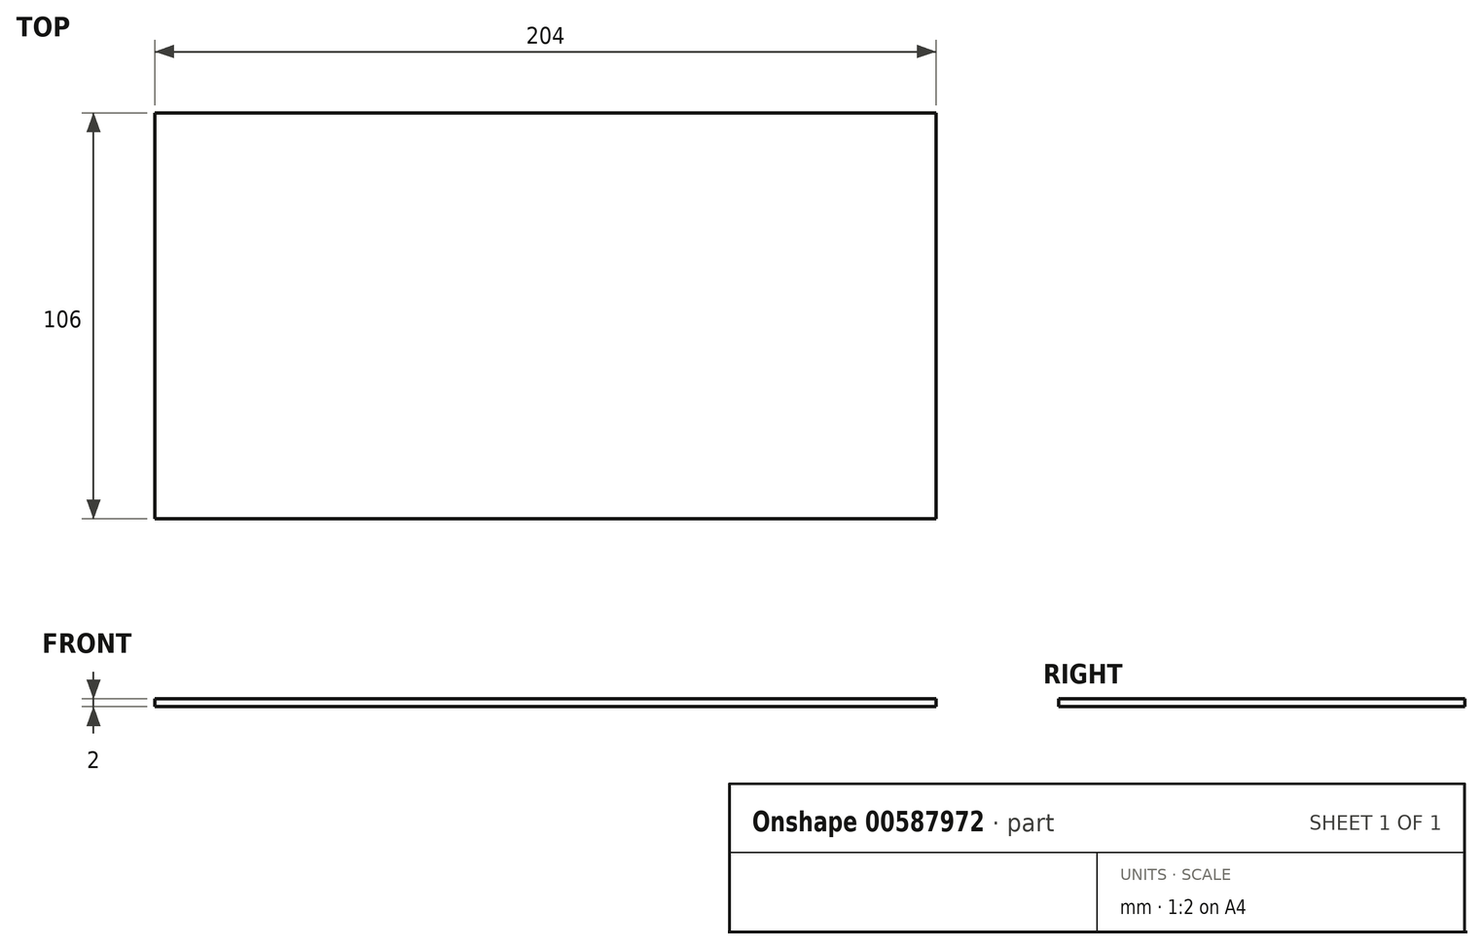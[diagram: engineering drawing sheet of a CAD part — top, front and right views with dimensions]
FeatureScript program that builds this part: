
annotation { "Feature Type Name" : "Feature", "Feature Type Description" : "" }
export const myFeature = defineFeature(function(context is Context, id is Id, definition is map)
    precondition{}
    {
        {
            var Q0;
            Q0=qCreatedBy(makeId("Top.planeOp"),FACE);
            var sketch = newSketch(context, id + "F0", { "sketchPlane" : qUnion([Q0])});
            skLineSegment(sketch, "E0.bottom", {"start": v(102, 53) * mm, "end": v(-102, 53) * mm});
            skLineSegment(sketch, "E0.top", {"start": v(102, -53) * mm, "end": v(-102, -53) * mm});
            skLineSegment(sketch, "E0.left", {"start": v(102, 53) * mm, "end": v(102, -53) * mm});
            skLineSegment(sketch, "E0.right", {"start": v(-102, 53) * mm, "end": v(-102, -53) * mm});
            skPoint(sketch, "E0.middle", {"position": v(0, 0) * mm});
            skSolve(sketch);
        }
        {
            var Q0;
            Q0=makeQuery(id+"F0.imprint","IMPRINT",FACE,{"disambiguationData":[TD([[makeQuery(id+"F0.imprint","IMPRINT",EDGE,{"derivedFrom":sQuery(id+"F0.wireOp",EDGE,"E0.bottom")}),1.0]])]});
            extrude(context, id + "F1", {"entities" : qUnion([Q0]), "depth" : 2 * mm, "offsetDistance" : 25 * mm});
        }
    });
